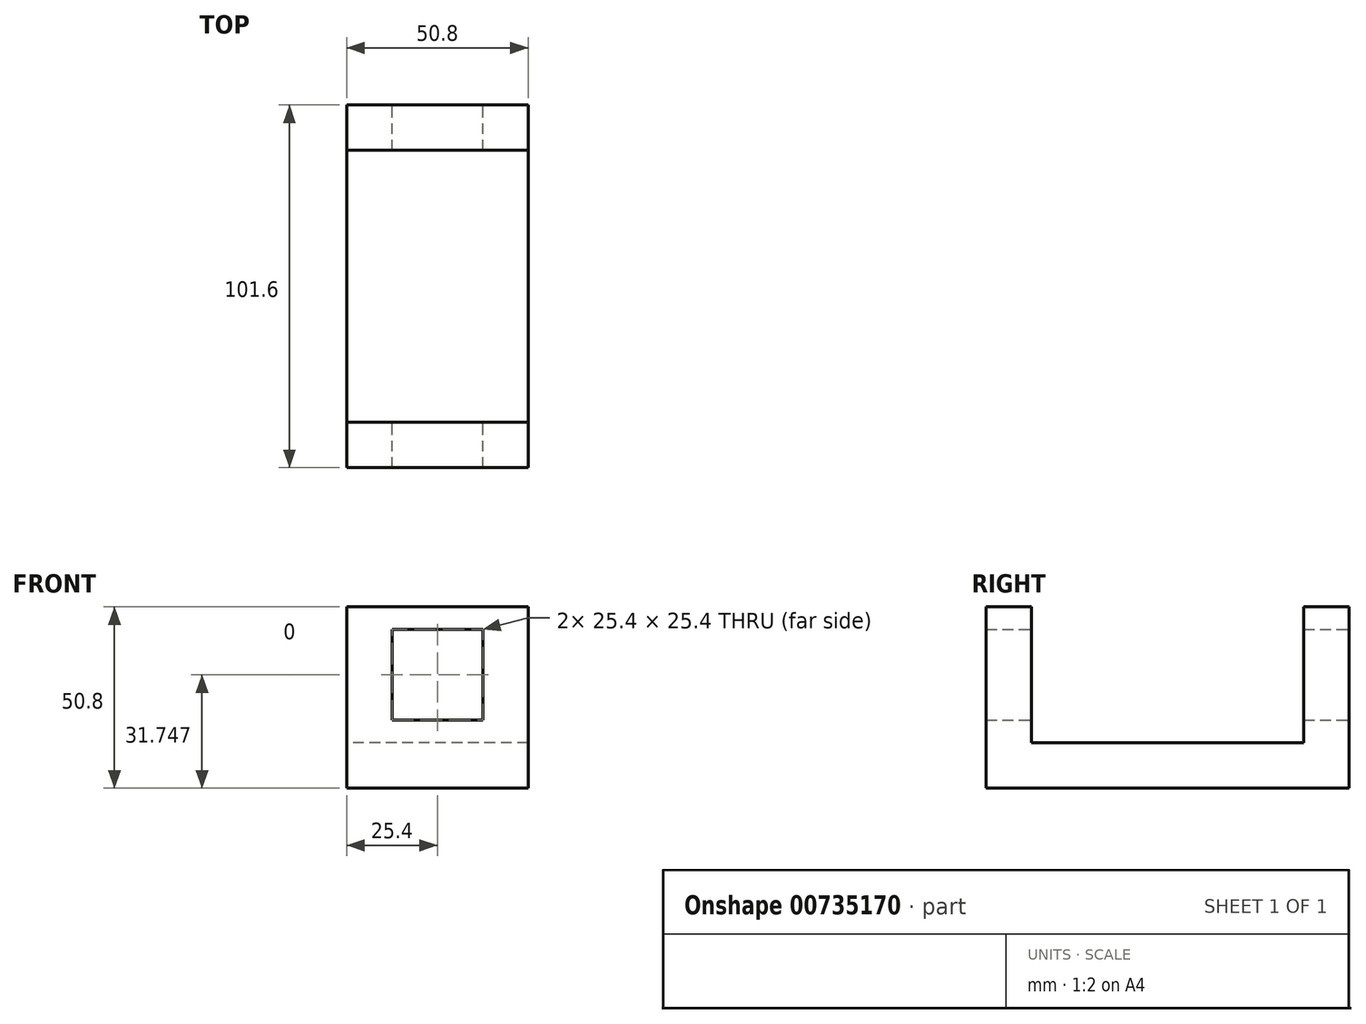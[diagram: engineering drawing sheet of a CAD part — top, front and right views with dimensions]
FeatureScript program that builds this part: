
annotation { "Feature Type Name" : "Feature", "Feature Type Description" : "" }
export const myFeature = defineFeature(function(context is Context, id is Id, definition is map)
    precondition{}
    {
        {
            var Q0;
            Q0=qCreatedBy(makeId("Right.planeOp"),FACE);
            var sketch = newSketch(context, id + "F0", { "sketchPlane" : qUnion([Q0])});
            skLineSegment(sketch, "E0", {"start": v(-39.98, -18.72) * mm, "end": v(48.92, -18.72) * mm});
            skLineSegment(sketch, "E1", {"start": v(48.92, -18.72) * mm, "end": v(48.92, 32.08) * mm});
            skLineSegment(sketch, "E2", {"start": v(48.92, 32.08) * mm, "end": v(36.22, 32.08) * mm});
            skLineSegment(sketch, "E3", {"start": v(36.22, 32.08) * mm, "end": v(36.22, -6.02) * mm});
            skLineSegment(sketch, "E4", {"start": v(36.22, -6.02) * mm, "end": v(-39.98, -6.02) * mm});
            skLineSegment(sketch, "E5", {"start": v(-39.98, -6.02) * mm, "end": v(-39.98, 32.08) * mm});
            skLineSegment(sketch, "E6", {"start": v(-39.98, 32.08) * mm, "end": v(-52.68, 32.08) * mm});
            skLineSegment(sketch, "E7", {"start": v(-52.68, 32.08) * mm, "end": v(-52.68, -18.72) * mm});
            skLineSegment(sketch, "E8", {"start": v(-52.68, -18.72) * mm, "end": v(-39.98, -18.72) * mm});
            skSolve(sketch);
        }
        {
            var Q0;
            Q0=makeQuery(id+"F0.imprint","IMPRINT",FACE,{"disambiguationData":[TD([[makeQuery(id+"F0.imprint","IMPRINT",EDGE,{"derivedFrom":sQuery(id+"F0.wireOp",EDGE,"E0")}),1.0]])]});
            extrude(context, id + "F1", {"entities" : qUnion([Q0]), "depth" : 50.8 * mm, "offsetDistance" : 25.4 * mm});
        }
        {
            var Q0;
            Q0=makeQuery(id+"F1.opExtrude","SWEPT_FACE",FACE,{"disambiguationData":[OSD([sQuery(id+"F0.wireOp",EDGE,"E7")])]});
            var sketch = newSketch(context, id + "F2", { "sketchPlane" : qUnion([Q0])});
            skLineSegment(sketch, "E9.bottom", {"start": v(38.1, 0.33) * mm, "end": v(12.7, 0.33) * mm});
            skLineSegment(sketch, "E9.top", {"start": v(38.1, 25.73) * mm, "end": v(12.7, 25.73) * mm});
            skLineSegment(sketch, "E9.left", {"start": v(38.1, 0.33) * mm, "end": v(38.1, 25.73) * mm});
            skLineSegment(sketch, "E9.right", {"start": v(12.7, 0.33) * mm, "end": v(12.7, 25.73) * mm});
            skPoint(sketch, "E9.middle", {"position": v(25.4, 13.03) * mm});
            skLineSegment(sketch, "E10", {"start": v(0, 9.82) * mm, "end": v(12.7, 9.82) * mm});
            skLineSegment(sketch, "E11", {"start": v(25.4, 32.08) * mm, "end": v(25.4, 25.73) * mm});
            skLineSegment(sketch, "E12", {"start": v(50.8, 6.68) * mm, "end": v(38.1, 13.03) * mm});
            skLineSegment(sketch, "E13", {"start": v(24.35, -18.72) * mm, "end": v(24.35, 0.33) * mm});
            skSolve(sketch);
        }
        {
            var Q0;
            Q0 = qSketchRegion(id + "F2", true);
            extrude(context, id + "F3", {"entities" : qUnion([Q0]), "operationType" : NewBodyOperationType.REMOVE, "endBound" : BoundingType.SYMMETRIC, "depth" : 228.6 * mm, "offsetDistance" : 25.4 * mm});
        }
    });
